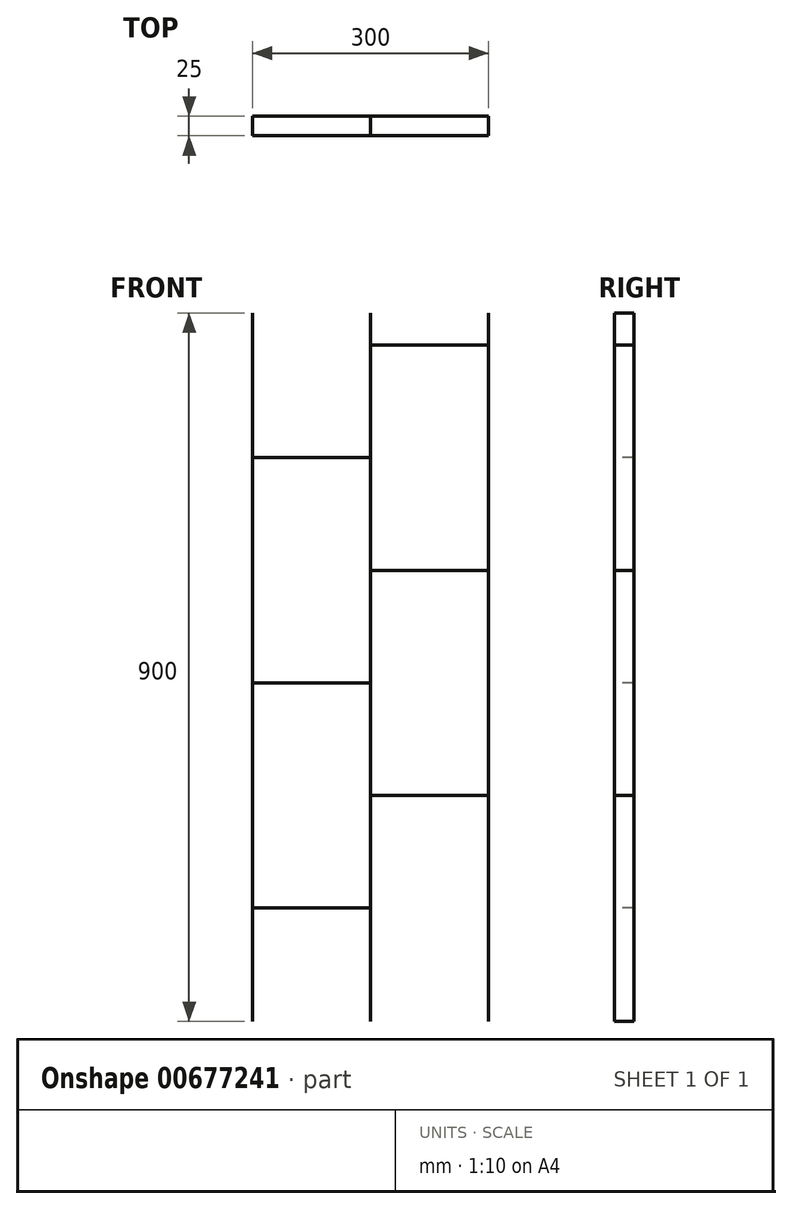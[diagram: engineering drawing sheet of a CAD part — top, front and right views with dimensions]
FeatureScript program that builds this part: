
annotation { "Feature Type Name" : "Feature", "Feature Type Description" : "" }
export const myFeature = defineFeature(function(context is Context, id is Id, definition is map)
    precondition{}
    {
        {
            var Q0;
            Q0=qCreatedBy(makeId("Front.planeOp"),FACE);
            var sketch = newSketch(context, id + "F0", { "sketchPlane" : qUnion([Q0])});
            skLineSegment(sketch, "E0.top", {"start": v(-250, -623.73) * mm, "end": v(250, -623.73) * mm});
            skLineSegment(sketch, "E0.left", {"start": v(-250, 276.27) * mm, "end": v(-250, -623.73) * mm});
            skLineSegment(sketch, "E0.right", {"start": v(250, 276.27) * mm, "end": v(250, -623.73) * mm});
            skLineSegment(sketch, "E1", {"start": v(-150, 276.27) * mm, "end": v(-150, -623.73) * mm});
            skLineSegment(sketch, "E2", {"start": v(0, 276.27) * mm, "end": v(0, -623.73) * mm});
            skLineSegment(sketch, "E3", {"start": v(150, 276.27) * mm, "end": v(150, -623.73) * mm});
            skLineSegment(sketch, "E4", {"start": v(150, 235.27) * mm, "end": v(0, 235.27) * mm});
            skLineSegment(sketch, "E5", {"start": v(150, -50.73) * mm, "end": v(0, -50.73) * mm});
            skLineSegment(sketch, "E6", {"start": v(150, -336.73) * mm, "end": v(0, -336.73) * mm});
            skLineSegment(sketch, "E7", {"start": v(-150, -479.73) * mm, "end": v(0, -479.73) * mm});
            skLineSegment(sketch, "E8", {"start": v(-150, -193.73) * mm, "end": v(0, -193.73) * mm});
            skLineSegment(sketch, "E9", {"start": v(-150, 92.27) * mm, "end": v(0, 92.27) * mm});
            skLineSegment(sketch, "E10", {"start": v(-250, 276.27) * mm, "end": v(250, 276.27) * mm});
            skSolve(sketch);
        }
        {
            var Q0;
            Q0=sQuery(id+"F0.wireOp",EDGE,"E4");
            var Q1;
            Q1=sQuery(id+"F0.wireOp",EDGE,"E9");
            var Q2;
            Q2=sQuery(id+"F0.wireOp",EDGE,"E5");
            var Q3;
            Q3=sQuery(id+"F0.wireOp",EDGE,"E8");
            var Q4;
            Q4=sQuery(id+"F0.wireOp",EDGE,"E6");
            var Q5;
            Q5=sQuery(id+"F0.wireOp",EDGE,"E7");
            extrude(context, id + "F1", {"bodyType" : ToolBodyType.SURFACE, "surfaceEntities" : qUnion([Q0, Q1, Q2, Q3, Q4, Q5]), "depth" : 25 * mm, "offsetDistance" : 25 * mm});
        }
        {
            var Q0;
            Q0=sQuery(id+"F0.wireOp",EDGE,"E1");
            var Q1;
            Q1=sQuery(id+"F0.wireOp",EDGE,"E2");
            var Q2;
            Q2=sQuery(id+"F0.wireOp",EDGE,"E3");
            extrude(context, id + "F2", {"bodyType" : ToolBodyType.SURFACE, "surfaceEntities" : qUnion([Q0, Q1, Q2]), "depth" : 25 * mm, "offsetDistance" : 25 * mm});
        }
    });
